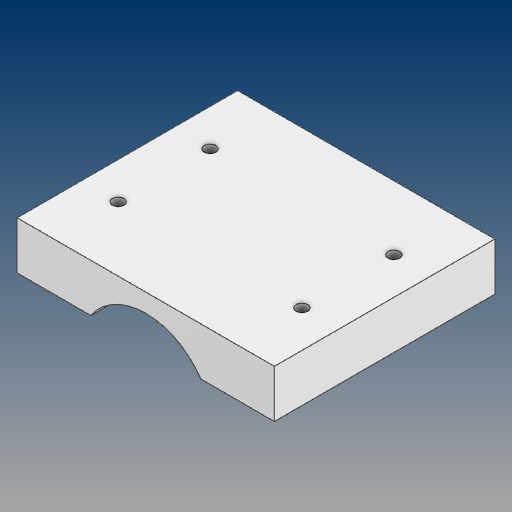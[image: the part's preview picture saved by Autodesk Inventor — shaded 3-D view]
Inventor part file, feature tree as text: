
AUTODESK INVENTOR PART (.ipt)
format: ipt  version: 2021 (Build 250183000, 183)  size: 117,760 bytes
history: native  units: mm
features: sketch x2, projected_geometry x2, extrude x1, hole x1
ambient origin geometry x8: Origin, YZ Plane, XZ Plane, XY Plane, X Axis, Y Axis, Z Axis, Center Point
bodies: Solid1 (feature_tree)
feature tree (6):
  extrude  "Extrusion1"  Depth=10.0mm
  hole  "Hole1"  [1 undecoded]
  sketch  "Sketch1"  dims[d0=36.0mm d1=10.0mm]
  sketch  "Sketch2"  dims[d2=70.0mm d3=13.0mm d4=60.0mm d5=0.0mm d6=25.0mm d7=3.2mm d8=6.0mm d9=4.0mm d10=2.0mm d11=90.0deg d12=8.0mm d13=20.594885mm]
  projected_geometry  "Projected Loop1"
  projected_geometry  "Projected Loop2"
note: 1 required parameter value undecoded (feature->parameter linkage not recoverable at this tier; creation-order binding heuristic only, values carry confidence <= 0.55)
